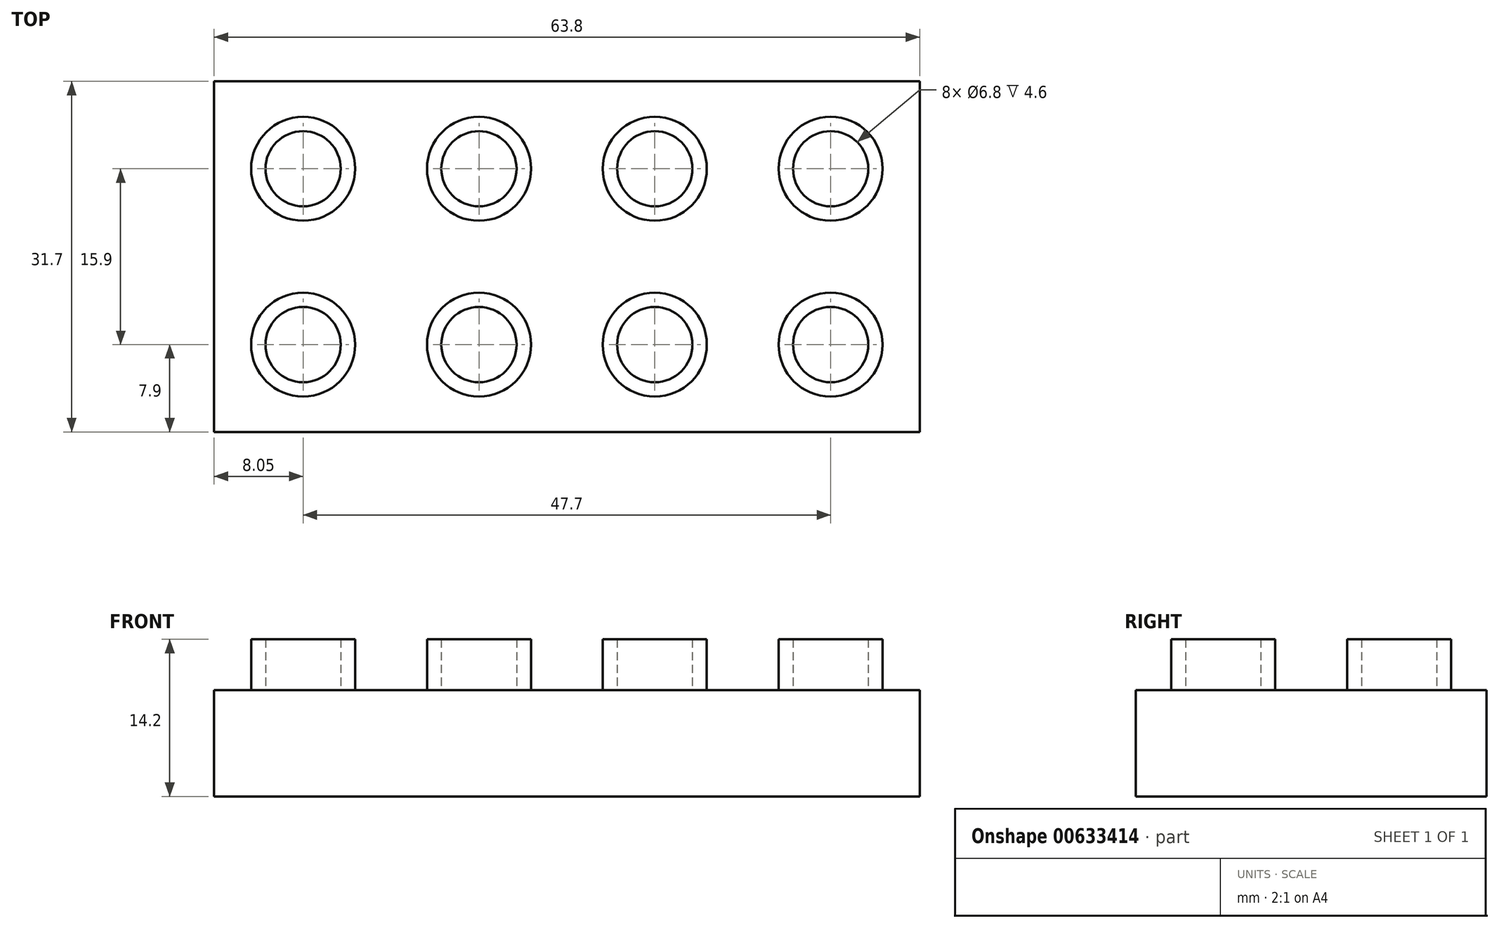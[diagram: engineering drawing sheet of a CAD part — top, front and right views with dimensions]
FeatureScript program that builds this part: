
annotation { "Feature Type Name" : "Feature", "Feature Type Description" : "" }
export const myFeature = defineFeature(function(context is Context, id is Id, definition is map)
    precondition{}
    {
        {
            var Q0;
            Q0=qCreatedBy(makeId("Top.planeOp"),FACE);
            var sketch = newSketch(context, id + "F0", { "sketchPlane" : qUnion([Q0])});
            skLineSegment(sketch, "E0.bottom", {"start": v(-31.9, 15.85) * mm, "end": v(31.9, 15.85) * mm});
            skLineSegment(sketch, "E0.top", {"start": v(-31.9, -15.85) * mm, "end": v(31.9, -15.85) * mm});
            skLineSegment(sketch, "E0.left", {"start": v(-31.9, 15.85) * mm, "end": v(-31.9, -15.85) * mm});
            skLineSegment(sketch, "E0.right", {"start": v(31.9, 15.85) * mm, "end": v(31.9, -15.85) * mm});
            skSolve(sketch);
        }
        {
            var Q0;
            Q0=qSketchRegion(id+"F0",true);
            extrude(context, id + "F1", {"entities" : qUnion([Q0]), "depth" : 9.6 * mm, "offsetDistance" : 25 * mm});
        }
        {
            var Q0;
            Q0=makeQuery(id+"F1.opExtrude","CAP_FACE",FACE,{"disambiguationData":[OSD([sQuery(id+"F0.wireOp",EDGE,"E0.bottom"),sQuery(id+"F0.wireOp",EDGE,"E0.top"),sQuery(id+"F0.wireOp",EDGE,"E0.left"),sQuery(id+"F0.wireOp",EDGE,"E0.right")])],"isStart":false});
            var sketch = newSketch(context, id + "F2", { "sketchPlane" : qUnion([Q0])});
            skCircle(sketch, "E1", {"center": v(7.95, 7.95) * mm, "radius": 3.4 * mm});
            skCircle(sketch, "E2", {"center": v(7.95, 7.95) * mm, "radius": 4.7 * mm});
            skCircle(sketch, "E3", {"center": v(-7.95, 7.95) * mm, "radius": 3.4 * mm});
            skCircle(sketch, "E4", {"center": v(-7.95, 7.95) * mm, "radius": 4.7 * mm});
            skCircle(sketch, "E5", {"center": v(-23.85, 7.95) * mm, "radius": 3.4 * mm});
            skCircle(sketch, "E6", {"center": v(-23.85, 7.95) * mm, "radius": 4.7 * mm});
            skCircle(sketch, "E7", {"center": v(23.85, 7.95) * mm, "radius": 3.4 * mm});
            skCircle(sketch, "E8", {"center": v(23.85, 7.95) * mm, "radius": 4.7 * mm});
            skCircle(sketch, "E9.MirrorC", {"center": v(23.85, -7.95) * mm, "radius": 3.4 * mm});
            skCircle(sketch, "E10.MirrorC", {"center": v(7.95, -7.95) * mm, "radius": 3.4 * mm});
            skCircle(sketch, "E11.MirrorC", {"center": v(7.95, -7.95) * mm, "radius": 4.7 * mm});
            skCircle(sketch, "E12.MirrorC", {"center": v(-23.85, -7.95) * mm, "radius": 4.7 * mm});
            skCircle(sketch, "E13.MirrorC", {"center": v(-7.95, -7.95) * mm, "radius": 3.4 * mm});
            skCircle(sketch, "E14.MirrorC", {"center": v(23.85, -7.95) * mm, "radius": 4.7 * mm});
            skCircle(sketch, "E15.MirrorC", {"center": v(-23.85, -7.95) * mm, "radius": 3.4 * mm});
            skCircle(sketch, "E16.MirrorC", {"center": v(-7.95, -7.95) * mm, "radius": 4.7 * mm});
            skSolve(sketch);
        }
        {
            var Q0;
            Q0=qSketchRegion(id+"F2",true);
            extrude(context, id + "F3", {"entities" : qUnion([Q0]), "operationType" : NewBodyOperationType.ADD, "depth" : 4.6 * mm, "offsetDistance" : 25 * mm});
        }
    });
